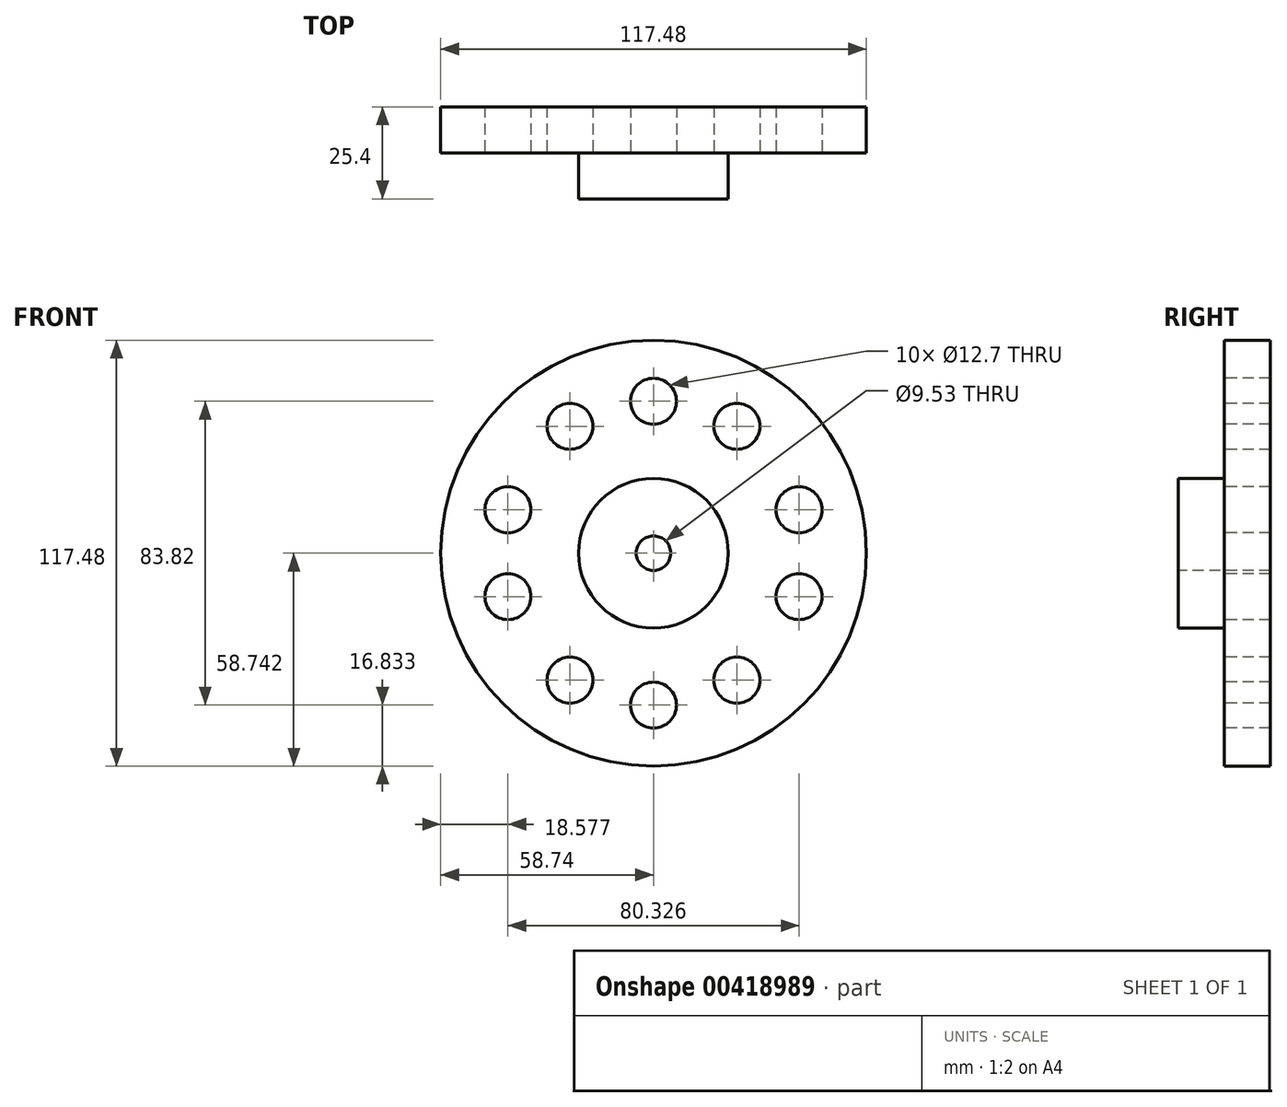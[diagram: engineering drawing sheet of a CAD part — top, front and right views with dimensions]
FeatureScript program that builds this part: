
annotation { "Feature Type Name" : "Feature", "Feature Type Description" : "" }
export const myFeature = defineFeature(function(context is Context, id is Id, definition is map)
    precondition{}
    {
        {
            var Q0;
            Q0=qCreatedBy(makeId("Right.planeOp"),FACE);
            var sketch = newSketch(context, id + "F0", { "sketchPlane" : qUnion([Q0])});
            skLineSegment(sketch, "E0", {"start": v(0, 0) * mm, "end": v(0, 9.53) * mm});
            skLineSegment(sketch, "E1", {"start": v(0, 9.53) * mm, "end": v(25.4, 9.53) * mm});
            skLineSegment(sketch, "E2", {"start": v(0, 9.53) * mm, "end": v(0, 25.4) * mm});
            skLineSegment(sketch, "E3", {"start": v(0, 25.4) * mm, "end": v(12.7, 25.4) * mm});
            skLineSegment(sketch, "E4", {"start": v(25.4, 9.53) * mm, "end": v(25.4, 63.5) * mm});
            skLineSegment(sketch, "E5", {"start": v(25.4, 63.5) * mm, "end": v(12.7, 63.5) * mm});
            skLineSegment(sketch, "E6", {"start": v(12.7, 63.5) * mm, "end": v(12.7, 25.4) * mm});
            skLineSegment(sketch, "E7", {"start": v(0, 4.76) * mm, "end": v(25.4, 4.76) * mm});
            skPoint(sketch, "E7.endSnap0", {"position": v(25.4, 36.51) * mm});
            skSolve(sketch);
        }
        {
            var Q0;
            Q0=makeQuery(id+"F0.imprint","IMPRINT",FACE,{"disambiguationData":[TD([[makeQuery(id+"F0.imprint","IMPRINT",EDGE,{"derivedFrom":sQuery(id+"F0.wireOp",EDGE,"E1")}),1.0]])]});
            var Q1;
            Q1=sQuery(id+"F0.wireOp",EDGE,"E7");
            revolve(context, id + "F1", {"entities" : qUnion([Q0]), "axis" : qUnion([Q1]), "revolveType" : RevolveType.FULL});
        }
        {
            var Q0;
            Q0=qCreatedBy(makeId("Front.planeOp"),FACE);
            cPlane(context, id + "F2", {"entities" : qUnion([Q0]), "cplaneType" : CPlaneType.OFFSET, "offset" : 12.7 * mm, "oppositeDirection" : true, "width" : 152.4 * mm, "height" : 152.4 * mm});
        }
        {
            var Q0;
            Q0=qCreatedBy(id+"F2.planeOp",FACE);
            var sketch = newSketch(context, id + "F3", { "sketchPlane" : qUnion([Q0])});
            skPoint(sketch, "E8", {"position": v(0, 4.76) * mm});
            skCircle(sketch, "E9", {"center": v(0, 4.76) * mm, "radius": 41.91 * mm});
            skPoint(sketch, "E10", {"position": v(23.03, 39.78) * mm});
            skPoint(sketch, "E11", {"position": v(-23.03, 39.78) * mm});
            skPoint(sketch, "E12", {"position": v(-40.16, 16.74) * mm});
            skPoint(sketch, "E13", {"position": v(40.16, 16.74) * mm});
            skPoint(sketch, "E14", {"position": v(-40.16, -7.21) * mm});
            skPoint(sketch, "E15", {"position": v(-23.03, -30.25) * mm});
            skPoint(sketch, "E16", {"position": v(0, -37.15) * mm});
            skPoint(sketch, "E17", {"position": v(23.03, -30.25) * mm});
            skPoint(sketch, "E18", {"position": v(40.16, -7.21) * mm});
            skSolve(sketch);
        }
        {
            var Q0;
            Q0=qCreatedBy(id+"F2.planeOp",FACE);
            var sketch = newSketch(context, id + "F4", { "sketchPlane" : qUnion([Q0])});
            skPoint(sketch, "E19", {"position": v(0, 46.67) * mm});
            skSolve(sketch);
        }
        {
            var Q0;
            Q0=sQuery(id+"F4.wireOp",VERTEX,"E19");
            var Q1;
            Q1=sQuery(id+"F3.wireOp",VERTEX,"E11");
            var Q2;
            Q2=sQuery(id+"F3.wireOp",VERTEX,"E12");
            var Q3;
            Q3=sQuery(id+"F3.wireOp",VERTEX,"E14");
            var Q4;
            Q4=sQuery(id+"F3.wireOp",VERTEX,"E15");
            var Q5;
            Q5=sQuery(id+"F3.wireOp",VERTEX,"E16");
            var Q6;
            Q6=sQuery(id+"F3.wireOp",VERTEX,"E17");
            var Q7;
            Q7=sQuery(id+"F3.wireOp",VERTEX,"E18");
            var Q8;
            Q8=sQuery(id+"F3.wireOp",VERTEX,"E13");
            var Q9;
            Q9=sQuery(id+"F3.wireOp",VERTEX,"E10");
            var Q10;
            Q10=makeQuery(id+"F1.opRevolve","SWEPT_BODY",BODY,{"disambiguationData":[OSD([sQuery(id+"F0.wireOp",EDGE,"E1"),sQuery(id+"F0.wireOp",EDGE,"E2"),sQuery(id+"F0.wireOp",EDGE,"E3"),sQuery(id+"F0.wireOp",EDGE,"E4"),sQuery(id+"F0.wireOp",EDGE,"E5"),sQuery(id+"F0.wireOp",EDGE,"E6")])]});
            hole(context, id + "F5", {"style" : HoleStyle.SIMPLE, "endStyle" : HoleEndStyle.THROUGH, "holeDiameter" : 12.7 * mm, "isTappedThrough" : true, "tappedDepth" : 12.7 * mm, "tapClearance" : 3, "locations" : qUnion([Q0, Q1, Q2, Q3, Q4, Q5, Q6, Q7, Q8, Q9]), "scope" : qUnion([Q10])});
        }
    });
